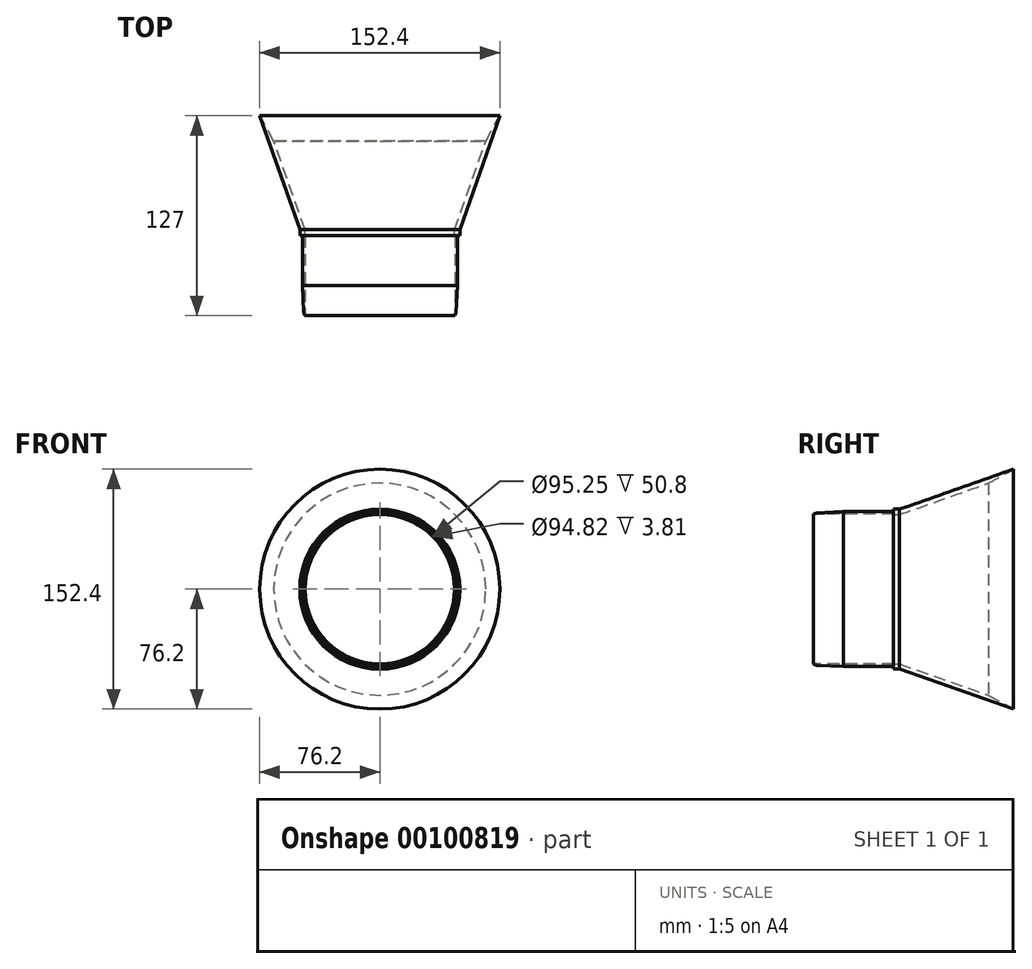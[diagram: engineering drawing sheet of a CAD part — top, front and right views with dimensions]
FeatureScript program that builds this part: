
annotation { "Feature Type Name" : "Feature", "Feature Type Description" : "" }
export const myFeature = defineFeature(function(context is Context, id is Id, definition is map)
    precondition{}
    {
        {
            var Q0;
            Q0=qCreatedBy(makeId("Front.planeOp"),FACE);
            var sketch = newSketch(context, id + "F0", { "sketchPlane" : qUnion([Q0])});
            skCircle(sketch, "E0", {"center": v(0, 0) * mm, "radius": 50.8 * mm});
            skCircle(sketch, "E1", {"center": v(0, 0) * mm, "radius": 47.63 * mm});
            skSolve(sketch);
        }
        {
            var Q0;
            Q0=qSketchRegion(id+"F0",true);
            extrude(context, id + "F1", {"entities" : qUnion([Q0]), "oppositeDirection" : true, "depth" : 3.8 * mm, "hasSecondDirection" : true, "secondDirectionOppositeDirection" : false, "secondDirectionDepth" : 50.8 * mm});
        }
        {
            var Q0;
            Q0=qCreatedBy(makeId("Front.planeOp"),FACE);
            var sketch = newSketch(context, id + "F2", { "sketchPlane" : qUnion([Q0])});
            skCircle(sketch, "E2", {"center": v(0, 0) * mm, "radius": 49.21 * mm});
            skCircle(sketch, "E3", {"center": v(0, 0) * mm, "radius": 50.8 * mm});
            skSolve(sketch);
        }
        {
            var Q0;
            Q0=qSketchRegion(id+"F2",true);
            extrude(context, id + "F3", {"entities" : qUnion([Q0]), "operationType" : NewBodyOperationType.REMOVE, "endBound" : BoundingType.THROUGH_ALL, "depth" : 25.4 * mm});
        }
        {
            var Q0;
            Q0=makeQuery(id+"F3.boolean.opBoolean","INTERSECT",EDGE,{"derivedFrom":[makeQuery(id+"F1.opExtrude","CAP_FACE",FACE,{"disambiguationData":[OSD([sQuery(id+"F0.wireOp",EDGE,"E0"),sQuery(id+"F0.wireOp",EDGE,"E1")])],"isStart":true}),makeQuery(id+"F3.opExtrude","SWEPT_FACE",FACE,{"disambiguationData":[OSD([sQuery(id+"F2.wireOp",EDGE,"E2")])]})]});
            chamfer(context, id + "F4", {"entities" : qUnion([Q0]), "chamferType" : ChamferType.TWO_OFFSETS, "width1" : 19.05 * mm, "oppositeDirection" : false, "width2" : 1.02 * mm, "tangentPropagation" : true});
        }
        {
            var Q0;
            {var subQ0=makeQuery(id+"F1.opExtrude","CAP_FACE",FACE,{"disambiguationData":[OSD([sQuery(id+"F0.wireOp",EDGE,"E0"),sQuery(id+"F0.wireOp",EDGE,"E1")])],"isStart":true});Q0=makeQuery(id+"F4.opChamfer","BLEND_EDGE",EDGE,{"blendedFrom":[makeQuery(id+"F3.boolean.opBoolean","INTERSECT",EDGE,{"derivedFrom":[subQ0,makeQuery(id+"F3.opExtrude","SWEPT_FACE",FACE,{"disambiguationData":[OSD([sQuery(id+"F2.wireOp",EDGE,"E2")])]})]}),subQ0],"blendedInto":[subQ0]});}
            fillet(context, id + "F5", {"entities" : qUnion([Q0]), "radius" : 5.08 * mm, "tangentPropagation" : true, "allowEdgeOverflow" : false});
        }
        {
            var Q0;
            Q0=qCreatedBy(makeId("Right.planeOp"),FACE);
            var sketch = newSketch(context, id + "F6", { "sketchPlane" : qUnion([Q0])});
            skLineSegment(sketch, "E4", {"start": v(3.8, 50.8) * mm, "end": v(76.2, 76.2) * mm});
            skLineSegment(sketch, "E5", {"start": v(76.2, 0) * mm, "end": v(0, 0) * mm});
            skLineSegment(sketch, "E6", {"start": v(0, 0) * mm, "end": v(0, 50.8) * mm});
            skLineSegment(sketch, "E7", {"start": v(0, 50.8) * mm, "end": v(3.81, 50.8) * mm});
            skLineSegment(sketch, "E8", {"start": v(60.26, 67.33) * mm, "end": v(3.8, 47.4) * mm});
            skLineSegment(sketch, "E9", {"start": v(3.81, 47.4) * mm, "end": v(0, 47.4) * mm});
            skLineSegment(sketch, "E10", {"start": v(76.2, 76.2) * mm, "end": v(60.26, 67.33) * mm});
            skSolve(sketch);
        }
        {
            var Q0;
            Q0=makeQuery(id+"F6.imprint","IMPRINT",FACE,{"disambiguationData":[TD([[makeQuery(id+"F6.imprint","IMPRINT",EDGE,{"derivedFrom":sQuery(id+"F6.wireOp",EDGE,"E4")}),-1.0]])]});
            var Q1;
            Q1=sQuery(id+"F6.wireOp",EDGE,"E5");
            revolve(context, id + "F7", {"operationType" : NewBodyOperationType.ADD, "entities" : qUnion([Q0]), "axis" : qUnion([Q1]), "revolveType" : RevolveType.FULL});
        }
    });
